# Revit family: QF_T&S_B-0230-LN
name_source: partatom
category: Specialty Equipment
revit_build: Autodesk Revit Architecture 2012 (Build: 20110916_2132(x64)
units: mm (PartAtom-declared; Revit-internal decimal feet)

## types (1)
- QF_T&S_B-0230-LN
    Cold Water Connection Height = 0"
    Cold Water Consumption = 28.630 GPM
    Cold Water Flow = 28.63 GPM
    Cold Water Inlet Flow = 28.63 GPM
    Cold Water Maximum Pressure = 125.00 psi
    Cold Water Minimum Pressure = 20.00 psi
    Cold Water RI Height = 0"
    Cold Water Size = 1"
    Cold Water Temperature Recommended = 40 °F
    Connector 1 Description = Cold Water Inlet
    Connector 2 Description = Hot Water Inlet
    Description = 8'' Wall Mount Mixing Faucet, Eterna Cartridges, Lever Handles & 1/2'' NPT Female Inlets, Less Nozzle
    Faucet Material = Metal-T&S Brass-Chrome Plated Brass
    Foodservice Equipment Identifier = Yes
    Hot Water Connection Height = 0"
    Hot Water Consumption = 28.63 GPM
    Hot Water Flow = 28.63 GPM
    Hot Water Inlet Flow = 28.63 GPM
    Hot Water Maximum Pressure = 125.00 psi
    Hot Water Minimum Pressure = 20.00 psi
    Hot Water RI Height = 0"
    Hot Water Size = 1"
    Hot Water Temperature = 140 °F
    Identify Quantity as Lot = Yes
    Manufacturer = T&S Brass and Bronze Works, Inc.
    Manufacturer Fax = 1-800-868-0084
    Model = B-0230-LN
    Plumbing Remarks = Pressure: 20 - 125 psi, Temperature: 40 °F - 140 °F, Flow Rate: 28.63 GPM @ 60 psi / Outlet device andor final configuration may reduce flow rate.
    Product Documentation Link = http://catalog.tsbrass.com
    Product Page URL = http://www.tsbrass.com
    URL = http://www.tsbrass.com
    Water Supply Radius = 1/4"
    Weight in Pounds = 0

## geometry (parser evidence)
native form markers: Blend x10, Sweep x5
no freeform markers — native parametric forms only
